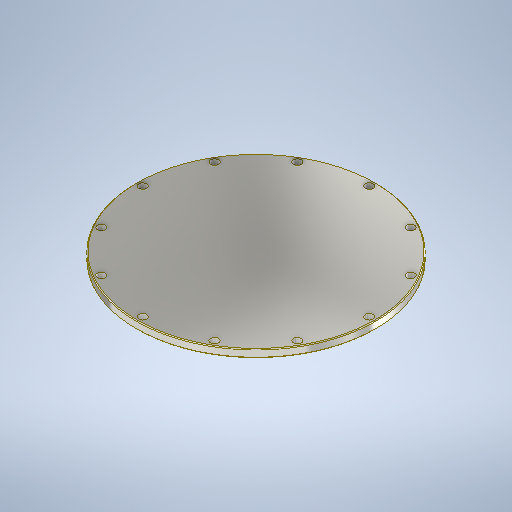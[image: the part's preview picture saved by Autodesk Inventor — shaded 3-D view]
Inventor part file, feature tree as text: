
AUTODESK INVENTOR PART (.ipt)
format: ipt  version: 2025.1 (Build 291241000, 241)  size: 292,864 bytes
history: native  units: mm
features: sketch x2, extrude x1, hole x1, pattern_circular x1, fillet x1
ambient origin geometry x8: Origin, YZ Plane, XZ Plane, XY Plane, X Axis, Y Axis, Z Axis, Center Point
bodies: Solid1 (feature_tree)
feature tree (6):
  extrude  "Extrusion1"  Depth=5.0mm TaperAngle=0.0deg
  hole  "Hole1"  [1 undecoded]
  pattern_circular  "Circular Pattern1"  [2 undecoded]
  fillet  "Fillet1"  [1 undecoded]
  sketch  "Sketch1"  dims[d0=151.0mm d1=5.0mm d2=0.0mm]
  sketch  "Sketch2"  dims[d3=143.0mm d4=5.0mm d5=6.0mm d6=4.0mm d7=2.0mm d8=90.0deg d9=8.0mm d10=0.0mm d11=120.0mm d12=360.0deg d14=0.5mm]
note: 4 required parameter values undecoded (feature->parameter linkage not recoverable at this tier; creation-order binding heuristic only, values carry confidence <= 0.55)
